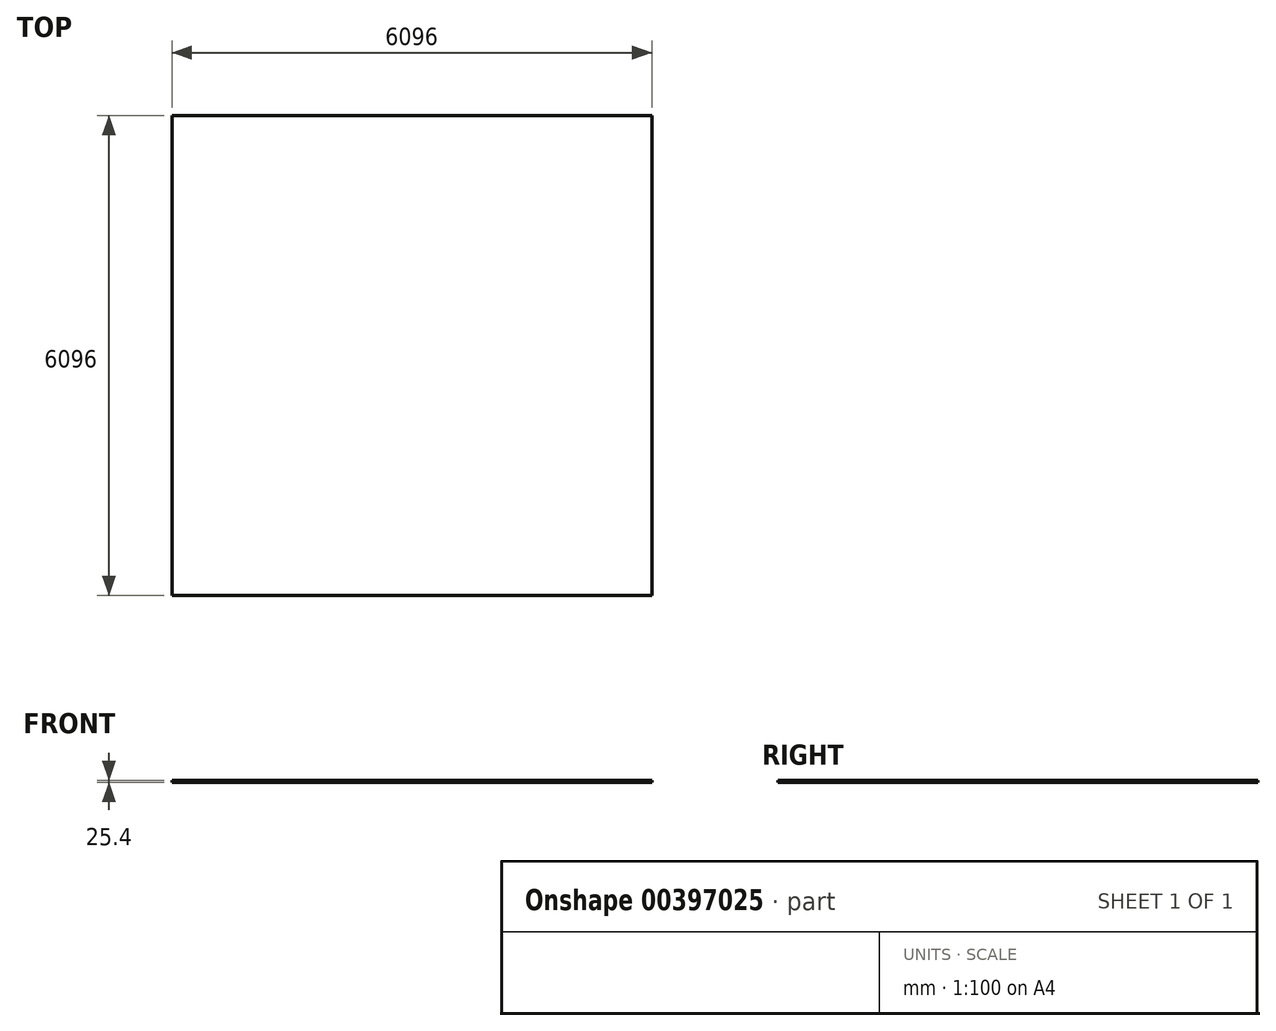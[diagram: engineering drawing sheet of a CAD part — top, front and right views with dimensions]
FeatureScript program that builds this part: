
annotation { "Feature Type Name" : "Feature", "Feature Type Description" : "" }
export const myFeature = defineFeature(function(context is Context, id is Id, definition is map)
    precondition{}
    {
        {
            var Q0;
            Q0=qCreatedBy(makeId("Top.planeOp"),FACE);
            var sketch = newSketch(context, id + "F0", { "sketchPlane" : qUnion([Q0])});
            skLineSegment(sketch, "E0.bottom", {"start": v(-3048, -3048) * mm, "end": v(3048, -3048) * mm});
            skLineSegment(sketch, "E0.top", {"start": v(-3048, 3048) * mm, "end": v(3048, 3048) * mm});
            skLineSegment(sketch, "E0.left", {"start": v(-3048, -3048) * mm, "end": v(-3048, 3048) * mm});
            skLineSegment(sketch, "E0.right", {"start": v(3048, -3048) * mm, "end": v(3048, 3048) * mm});
            skLineSegment(sketch, "E1", {"start": v(0, 3048) * mm, "end": v(0, -3048) * mm, "construction": true});
            skLineSegment(sketch, "E2", {"start": v(-3048, 0) * mm, "end": v(3048, 0) * mm, "construction": true});
            skSolve(sketch);
        }
        {
            var Q0;
            Q0 = qSketchRegion(id + "F0", true);
            extrude(context, id + "F1", {"entities" : qUnion([Q0]), "depth" : 25.4 * mm});
        }
    });
